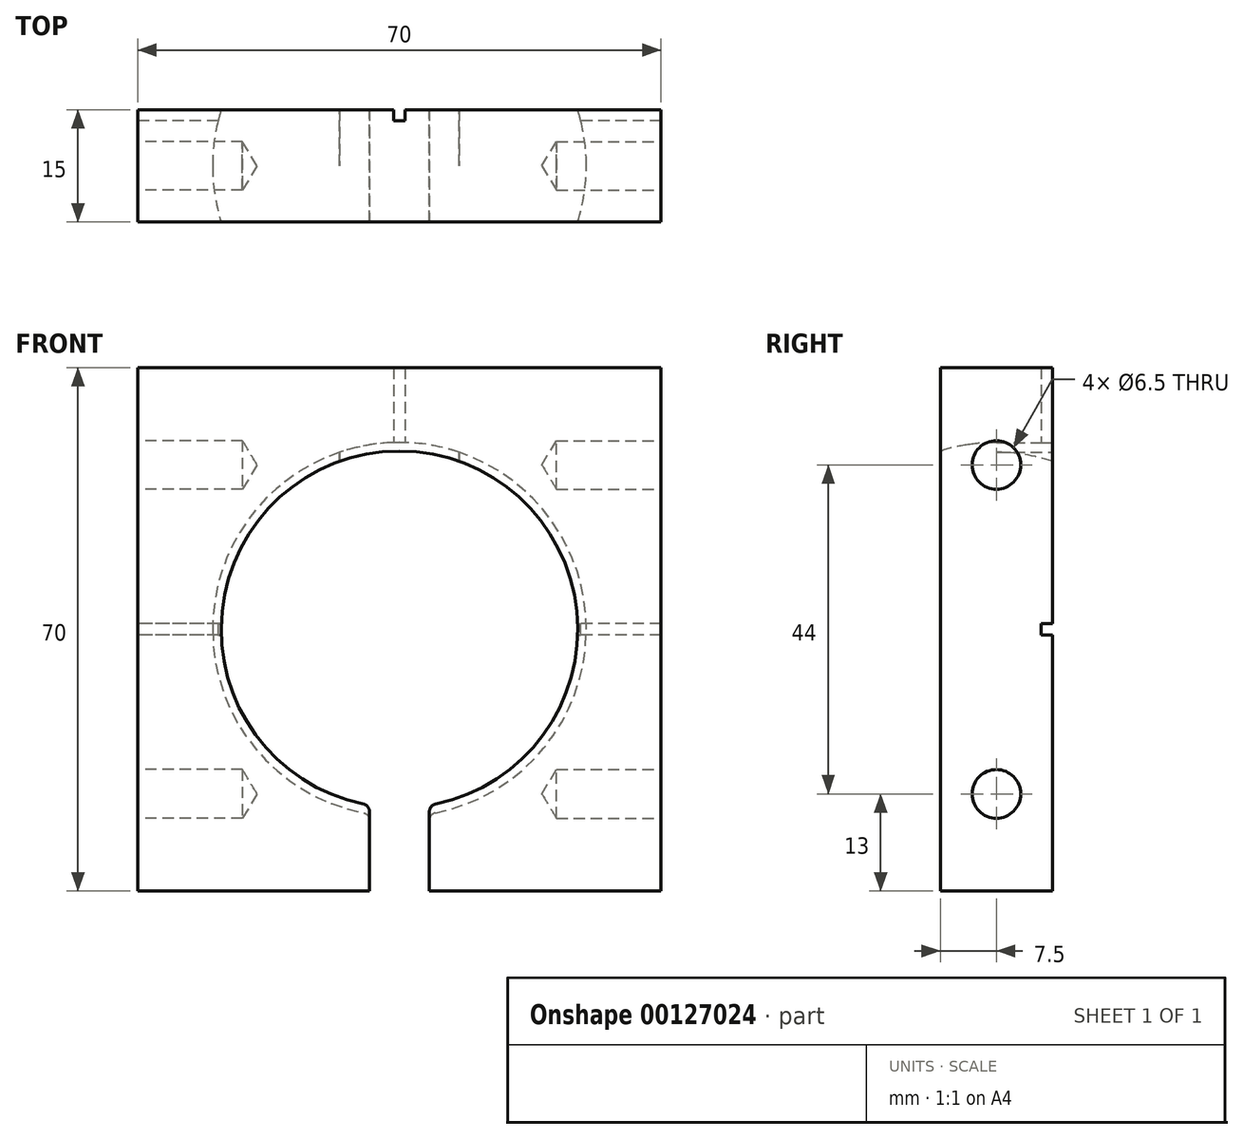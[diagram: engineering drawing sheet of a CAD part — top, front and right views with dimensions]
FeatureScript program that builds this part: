
annotation { "Feature Type Name" : "Feature", "Feature Type Description" : "" }
export const myFeature = defineFeature(function(context is Context, id is Id, definition is map)
    precondition{}
    {
        {
            var Q0;
            Q0=qCreatedBy(makeId("Front.planeOp"),FACE);
            var sketch = newSketch(context, id + "F0", { "sketchPlane" : qUnion([Q0])});
            skLineSegment(sketch, "E0.bottom", {"start": v(-30, 30) * mm, "end": v(30, 30) * mm});
            skLineSegment(sketch, "E0.top", {"start": v(-30, -30) * mm, "end": v(30, -30) * mm});
            skLineSegment(sketch, "E0.left", {"start": v(-30, 30) * mm, "end": v(-30, -30) * mm});
            skLineSegment(sketch, "E0.right", {"start": v(30, 30) * mm, "end": v(30, -30) * mm});
            skPoint(sketch, "E0.middle", {"position": v(0, 0) * mm});
            skSolve(sketch);
        }
        {
            var Q0;
            Q0=qSketchRegion(id+"F0",true);
            extrude(context, id + "F1", {"entities" : qUnion([Q0]), "endBound" : BoundingType.SYMMETRIC, "depth" : 15 * mm});
        }
        {
            var Q0;
            Q0=qCreatedBy(makeId("Front.planeOp"),FACE);
            var sketch = newSketch(context, id + "F2", { "sketchPlane" : qUnion([Q0])});
            skArc(sketch, "E1", {"start": v(25, 0) * mm, "mid": v(0, 25) * mm, "end": v(-25, 0) * mm});
            skLineSegment(sketch, "E2", {"start": v(-38.9, 0) * mm, "end": v(39.31, 0) * mm});
            skSolve(sketch);
        }
        {
            var Q0;
            Q0=qSketchRegion(id+"F2",true);
            var Q1;
            Q1=sQuery(id+"F2.wireOp",EDGE,"E2");
            revolve(context, id + "F3", {"operationType" : NewBodyOperationType.REMOVE, "entities" : qUnion([Q0]), "axis" : qUnion([Q1]), "revolveType" : RevolveType.FULL, "oppositeDirection" : true});
        }
        {
            var Q0;
            Q0=makeQuery(id+"F1.opExtrude","SWEPT_FACE",FACE,{"disambiguationData":[OSD([sQuery(id+"F0.wireOp",EDGE,"E0.top")])]});
            var sketch = newSketch(context, id + "F4", { "sketchPlane" : qUnion([Q0])});
            skLineSegment(sketch, "E3.bottom", {"start": v(-4, 16.93) * mm, "end": v(4, 16.93) * mm});
            skLineSegment(sketch, "E3.top", {"start": v(-4, -16.93) * mm, "end": v(4, -16.93) * mm});
            skLineSegment(sketch, "E3.left", {"start": v(-4, 16.93) * mm, "end": v(-4, -16.93) * mm});
            skLineSegment(sketch, "E3.right", {"start": v(4, 16.93) * mm, "end": v(4, -16.93) * mm});
            skPoint(sketch, "E3.middle", {"position": v(0, 0) * mm});
            skSolve(sketch);
        }
        {
            var Q0;
            Q0=qSketchRegion(id+"F4",true);
            extrude(context, id + "F5", {"entities" : qUnion([Q0]), "operationType" : NewBodyOperationType.REMOVE, "oppositeDirection" : true, "depth" : 25 * mm});
        }
        {
            var Q0;
            Q0=makeQuery(id+"F1.opExtrude","SWEPT_FACE",FACE,{"disambiguationData":[OSD([sQuery(id+"F0.wireOp",EDGE,"E0.right")])]});
            var sketch = newSketch(context, id + "F6", { "sketchPlane" : qUnion([Q0])});
            skPoint(sketch, "E4", {"position": v(0, 22) * mm});
            skPoint(sketch, "E5", {"position": v(0, -22) * mm});
            skSolve(sketch);
        }
        {
            var Q0;
            Q0=sQuery(id+"F6.wireOp",VERTEX,"E4");
            var Q1;
            Q1=sQuery(id+"F6.wireOp",VERTEX,"E5");
            var Q2;
            Q2=makeQuery(id+"F1.opExtrude","SWEPT_BODY",BODY,{"disambiguationData":[OSD([sQuery(id+"F0.wireOp",EDGE,"E0.bottom"),sQuery(id+"F0.wireOp",EDGE,"E0.top"),sQuery(id+"F0.wireOp",EDGE,"E0.left"),sQuery(id+"F0.wireOp",EDGE,"E0.right")])]});
            hole(context, id + "F7", {"style" : HoleStyle.SIMPLE, "endStyle" : HoleEndStyle.BLIND, "holeDiameter" : 6.5 * mm, "holeDepth" : 9 * mm, "startFromSketch" : true, "locations" : qUnion([Q0, Q1]), "scope" : qUnion([Q2])});
        }
        {
            var Q0;
            Q0=makeQuery(id+"F1.opExtrude","CAP_FACE",FACE,{"disambiguationData":[OSD([sQuery(id+"F0.wireOp",EDGE,"E0.bottom"),sQuery(id+"F0.wireOp",EDGE,"E0.top"),sQuery(id+"F0.wireOp",EDGE,"E0.left"),sQuery(id+"F0.wireOp",EDGE,"E0.right")])],"isStart":true});
            var sketch = newSketch(context, id + "F8", { "sketchPlane" : qUnion([Q0])});
            skCircle(sketch, "E6", {"center": v(0, 0) * mm, "radius": 25 * mm});
            skLineSegment(sketch, "E7", {"start": v(-8, 23.69) * mm, "end": v(-8, 0) * mm});
            skLineSegment(sketch, "E8", {"start": v(8, 23.69) * mm, "end": v(8, 0) * mm});
            skLineSegment(sketch, "E9", {"start": v(-8, 0) * mm, "end": v(8, 0) * mm});
            skSolve(sketch);
        }
        {
            var Q0;
            {var subQ0=sQuery(id+"F8.wireOp",EDGE,"E7");var subQ1=sQuery(id+"F8.wireOp",EDGE,"E6");var subQ2=makeQuery(id+"F8.imprint","INTERSECT",VERTEX,{"derivedFrom":[subQ1,subQ0]});Q0=makeQuery(id+"F8.imprint","IMPRINT",FACE,{"disambiguationData":[TD([[makeQuery(id+"F8.imprint","IMPRINT",EDGE,{"disambiguationData":[TD([[subQ2,1.0]])],"derivedFrom":subQ1}),1.0]])]});}
            extrude(context, id + "F9", {"entities" : qUnion([Q0]), "operationType" : NewBodyOperationType.REMOVE, "oppositeDirection" : true, "depth" : 7.5 * mm});
        }
        {
            var Q0;
            Q0=makeQuery(id+"F1.opExtrude","SWEPT_FACE",FACE,{"disambiguationData":[OSD([sQuery(id+"F0.wireOp",EDGE,"E0.left")])]});
            var sketch = newSketch(context, id + "F10", { "sketchPlane" : qUnion([Q0])});
            skPoint(sketch, "E10", {"position": v(0, 22) * mm});
            skPoint(sketch, "E11", {"position": v(0, -22) * mm});
            skSolve(sketch);
        }
        {
            var Q0;
            Q0=sQuery(id+"F10.wireOp",VERTEX,"E10");
            var Q1;
            Q1=sQuery(id+"F10.wireOp",VERTEX,"E11");
            var Q2;
            Q2=makeQuery(id+"F1.opExtrude","SWEPT_BODY",BODY,{"disambiguationData":[OSD([sQuery(id+"F0.wireOp",EDGE,"E0.bottom"),sQuery(id+"F0.wireOp",EDGE,"E0.top"),sQuery(id+"F0.wireOp",EDGE,"E0.left"),sQuery(id+"F0.wireOp",EDGE,"E0.right")])]});
            hole(context, id + "F11", {"style" : HoleStyle.SIMPLE, "endStyle" : HoleEndStyle.BLIND, "holeDiameter" : 6.5 * mm, "holeDepth" : 9 * mm, "startFromSketch" : true, "locations" : qUnion([Q0, Q1]), "scope" : qUnion([Q2])});
        }
        {
            var Q0;
            Q0=makeQuery(id+"F5.boolean.opBoolean","INTERSECT",EDGE,{"derivedFrom":[makeQuery(id+"F3.boolean.opBoolean","COPY",FACE,{"derivedFrom":makeQuery(id+"F3.opRevolve","SWEPT_FACE",FACE,{"disambiguationData":[OSD([sQuery(id+"F2.wireOp",EDGE,"E1")])]})}),makeQuery(id+"F5.opExtrude","SWEPT_FACE",FACE,{"disambiguationData":[OSD([sQuery(id+"F4.wireOp",EDGE,"E3.left")])]})]});
            var Q1;
            Q1=makeQuery(id+"F5.boolean.opBoolean","INTERSECT",EDGE,{"derivedFrom":[makeQuery(id+"F3.boolean.opBoolean","COPY",FACE,{"derivedFrom":makeQuery(id+"F3.opRevolve","SWEPT_FACE",FACE,{"disambiguationData":[OSD([sQuery(id+"F2.wireOp",EDGE,"E1")])]})}),makeQuery(id+"F5.opExtrude","SWEPT_FACE",FACE,{"disambiguationData":[OSD([sQuery(id+"F4.wireOp",EDGE,"E3.right")])]})]});
            fillet(context, id + "F12", {"entities" : qUnion([Q0, Q1]), "radius" : 1 * mm, "tangentPropagation" : true, "allowEdgeOverflow" : false});
        }
        {
            var Q0;
            Q0=makeQuery(id+"F1.opExtrude","CAP_FACE",FACE,{"disambiguationData":[OSD([sQuery(id+"F0.wireOp",EDGE,"E0.bottom"),sQuery(id+"F0.wireOp",EDGE,"E0.top"),sQuery(id+"F0.wireOp",EDGE,"E0.left"),sQuery(id+"F0.wireOp",EDGE,"E0.right")])],"isStart":true});
            var sketch = newSketch(context, id + "F13", { "sketchPlane" : qUnion([Q0])});
            skLineSegment(sketch, "E12.bottom", {"start": v(-35, 0.75) * mm, "end": v(35, 0.75) * mm});
            skLineSegment(sketch, "E12.top", {"start": v(-35, -0.75) * mm, "end": v(35, -0.75) * mm});
            skLineSegment(sketch, "E12.left", {"start": v(-35, 0.75) * mm, "end": v(-35, -0.75) * mm});
            skLineSegment(sketch, "E12.right", {"start": v(35, 0.75) * mm, "end": v(35, -0.75) * mm});
            skPoint(sketch, "E12.middle", {"position": v(0, 0) * mm});
            skLineSegment(sketch, "E13.bottom", {"start": v(0.75, 39.08) * mm, "end": v(-0.75, 39.08) * mm});
            skLineSegment(sketch, "E13.top", {"start": v(0.75, -39.08) * mm, "end": v(-0.75, -39.08) * mm});
            skLineSegment(sketch, "E13.left", {"start": v(0.75, 39.08) * mm, "end": v(0.75, -39.08) * mm});
            skLineSegment(sketch, "E13.right", {"start": v(-0.75, 39.08) * mm, "end": v(-0.75, -39.08) * mm});
            skSolve(sketch);
        }
        {
            var Q0;
            Q0=qSketchRegion(id+"F13",true);
            extrude(context, id + "F14", {"entities" : qUnion([Q0]), "operationType" : NewBodyOperationType.REMOVE, "oppositeDirection" : true, "depth" : 1.5 * mm});
        }
        {
            var Q0;
            {var subQ1=sQuery(id+"F0.wireOp",EDGE,"E0.left");var subQ2=sQuery(id+"F0.wireOp",EDGE,"E0.top");Q0=makeQuery(id+"F5.boolean.opBoolean","SPLIT",FACE,{"disambiguationData":[TD([makeQuery(id+"F1.opExtrude","SWEPT_FACE",FACE,{"disambiguationData":[OSD([subQ1])]})])],"derivedFrom":makeQuery(id+"F1.opExtrude","SWEPT_FACE",FACE,{"disambiguationData":[OSD([subQ2])]})});}
            var Q1;
            {var subQ0=sQuery(id+"F0.wireOp",EDGE,"E0.right");var subQ2=sQuery(id+"F0.wireOp",EDGE,"E0.top");Q1=makeQuery(id+"F5.boolean.opBoolean","SPLIT",FACE,{"disambiguationData":[TD([makeQuery(id+"F1.opExtrude","SWEPT_FACE",FACE,{"disambiguationData":[OSD([subQ0])]})])],"derivedFrom":makeQuery(id+"F1.opExtrude","SWEPT_FACE",FACE,{"disambiguationData":[OSD([subQ2])]})});}
            extrude(context, id + "F15", {"entities" : qUnion([Q0, Q1]), "operationType" : NewBodyOperationType.ADD, "depth" : 5 * mm});
        }
        {
            var Q0;
            {var subQ0=sQuery(id+"F0.wireOp",EDGE,"E0.right");var subQ1=sQuery(id+"F0.wireOp",EDGE,"E0.left");var subQ2=sQuery(id+"F0.wireOp",EDGE,"E0.top");var subQ3=sQuery(id+"F0.wireOp",EDGE,"E0.bottom");var subQ4=makeQuery(id+"F1.opExtrude","CAP_FACE",FACE,{"disambiguationData":[OSD([subQ3,subQ2,subQ1,subQ0])],"isStart":false});var subQ6=makeQuery(id+"F1.opExtrude","SWEPT_FACE",FACE,{"disambiguationData":[OSD([subQ0])]});var subQ8=makeQuery(id+"F1.opExtrude","CAP_EDGE",EDGE,{"disambiguationData":[OSD([subQ2])],"isStart":false});var subQ9=makeQuery(id+"F1.opExtrude","SWEPT_FACE",FACE,{"disambiguationData":[OSD([subQ1])]});Q0=makeQuery(id+"F15.boolean.opBoolean","MERGE",FACE,{"derivedFrom":[makeQuery(id+"F2F2YNzaSMgMAiO_1.boolean.opBoolean","SPLIT",FACE,{"disambiguationData":[TD([makeQuery(id+"F1.opExtrude","SWEPT_FACE",FACE,{"disambiguationData":[OSD([subQ3])]})])],"derivedFrom":subQ4}),makeQuery(id+"F15.opExtrude","SWEPT_FACE",FACE,{"disambiguationData":[OSD([subQ2]),TDD([makeQuery(id+"F5.boolean.opBoolean","SPLIT",EDGE,{"disambiguationData":[TD([subQ9])],"derivedFrom":subQ8})])]}),makeQuery(id+"F15.opExtrude","SWEPT_FACE",FACE,{"disambiguationData":[OSD([subQ2]),TDD([makeQuery(id+"F5.boolean.opBoolean","SPLIT",EDGE,{"disambiguationData":[TD([subQ6])],"derivedFrom":subQ8})])]})]});}
            var sketch = newSketch(context, id + "F16", { "sketchPlane" : qUnion([Q0])});
            skLineSegment(sketch, "E14.bottom", {"start": v(-9, -27.36) * mm, "end": v(9, -27.36) * mm});
            skLineSegment(sketch, "E14.top", {"start": v(-9, -35) * mm, "end": v(9, -35) * mm});
            skLineSegment(sketch, "E14.left", {"start": v(-9, -27.36) * mm, "end": v(-9, -35) * mm});
            skLineSegment(sketch, "E14.right", {"start": v(9, -27.36) * mm, "end": v(9, -35) * mm});
            skSolve(sketch);
        }
        {
            var Q0;
            Q0=qSketchRegion(id+"F16",true);
            extrude(context, id + "F17", {"entities" : qUnion([Q0]), "operationType" : NewBodyOperationType.ADD, "depth" : 17 * mm});
        }
        {
            var Q0;
            Q0=makeQuery(id+"F17.opExtrude","SWEPT_FACE",FACE,{"disambiguationData":[OSD([sQuery(id+"F16.wireOp",EDGE,"E14.bottom")])]});
            extrude(context, id + "F18", {"entities" : qUnion([Q0]), "operationType" : NewBodyOperationType.REMOVE, "oppositeDirection" : true, "depth" : 25 * mm});
        }
        {
            var Q0;
            {var subQ0=sQuery(id+"F0.wireOp",EDGE,"E0.left");Q0=makeQuery(id+"F15.boolean.opBoolean","MERGE",FACE,{"derivedFrom":[makeQuery(id+"F1.opExtrude","SWEPT_FACE",FACE,{"disambiguationData":[OSD([subQ0])]}),makeQuery(id+"F15.opExtrude","SWEPT_FACE",FACE,{"disambiguationData":[OSD([sQuery(id+"F0.wireOp",EDGE,"E0.top"),subQ0])]})]});}
            extrude(context, id + "F19", {"entities" : qUnion([Q0]), "operationType" : NewBodyOperationType.ADD, "depth" : 5 * mm});
        }
        {
            var Q0;
            {var subQ0=sQuery(id+"F0.wireOp",EDGE,"E0.right");Q0=makeQuery(id+"F15.boolean.opBoolean","MERGE",FACE,{"derivedFrom":[makeQuery(id+"F1.opExtrude","SWEPT_FACE",FACE,{"disambiguationData":[OSD([subQ0])]}),makeQuery(id+"F15.opExtrude","SWEPT_FACE",FACE,{"disambiguationData":[OSD([sQuery(id+"F0.wireOp",EDGE,"E0.top"),subQ0])]})]});}
            extrude(context, id + "F20", {"entities" : qUnion([Q0]), "operationType" : NewBodyOperationType.ADD, "depth" : 5 * mm});
        }
        {
            var Q0;
            {var subQ0=sQuery(id+"F0.wireOp",EDGE,"E0.bottom");Q0=makeQuery(id+"F20.boolean.opBoolean","MERGE",FACE,{"derivedFrom":[makeQuery(id+"F19.boolean.opBoolean","MERGE",FACE,{"derivedFrom":[makeQuery(id+"F1.opExtrude","SWEPT_FACE",FACE,{"disambiguationData":[OSD([subQ0])]}),makeQuery(id+"F19.opExtrude","SWEPT_FACE",FACE,{"disambiguationData":[OSD([subQ0,sQuery(id+"F0.wireOp",EDGE,"E0.left")])]})]}),makeQuery(id+"F20.opExtrude","SWEPT_FACE",FACE,{"disambiguationData":[OSD([subQ0,sQuery(id+"F0.wireOp",EDGE,"E0.right")])]})]});}
            extrude(context, id + "F21", {"entities" : qUnion([Q0]), "operationType" : NewBodyOperationType.ADD, "depth" : 5 * mm});
        }
    });
